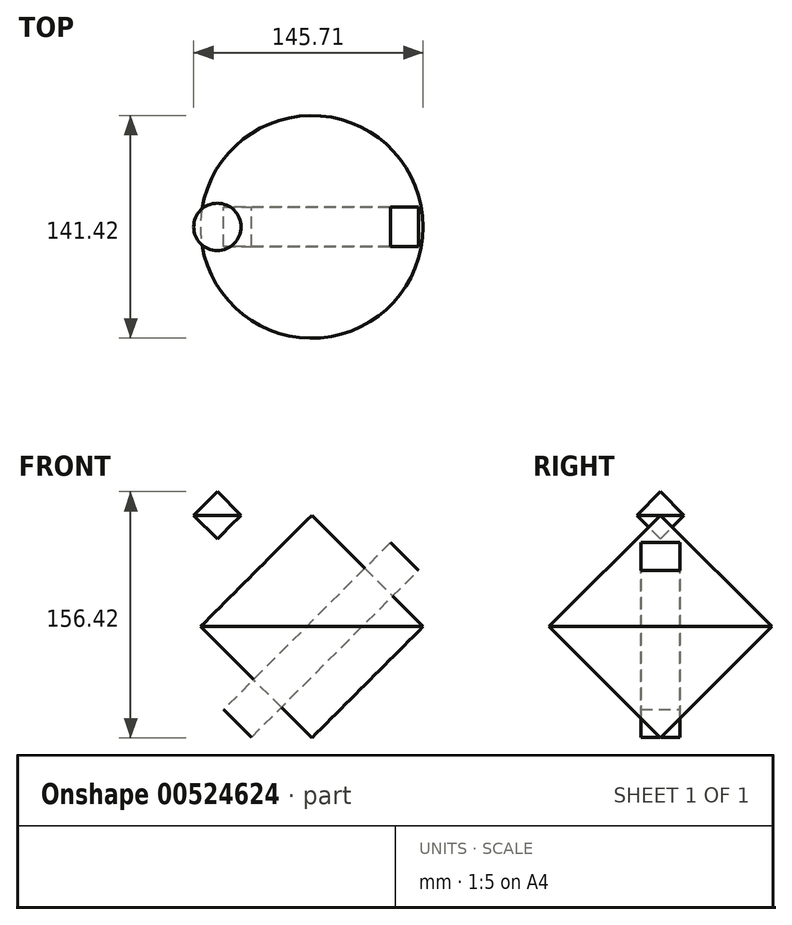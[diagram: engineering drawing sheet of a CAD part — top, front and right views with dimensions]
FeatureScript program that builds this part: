
annotation { "Feature Type Name" : "Feature", "Feature Type Description" : "" }
export const myFeature = defineFeature(function(context is Context, id is Id, definition is map)
    precondition{}
    {
        {
            var Q0;
            Q0=qCreatedBy(makeId("Front.planeOp"),FACE);
            var sketch = newSketch(context, id + "F0", { "sketchPlane" : qUnion([Q0])});
            skLineSegment(sketch, "E0", {"start": v(0, 80.4) * mm, "end": v(0, -82.74) * mm, "construction": true});
            skLineSegment(sketch, "E1", {"start": v(0, 70.71) * mm, "end": v(-70.71, 0) * mm});
            skLineSegment(sketch, "E2", {"start": v(-70.71, 0) * mm, "end": v(0, -70.71) * mm});
            skLineSegment(sketch, "E3", {"start": v(0, -70.71) * mm, "end": v(0, 70.71) * mm});
            skSolve(sketch);
        }
        {
            var Q0;
            Q0 = qSketchRegion(id + "F0", true);
            var Q1;
            Q1=sQuery(id+"F0.wireOp",EDGE,"E0");
            revolve(context, id + "F1", {"entities" : qUnion([Q0]), "axis" : qUnion([Q1]), "revolveType" : RevolveType.FULL});
        }
        {
            var Q0;
            Q0=qCreatedBy(makeId("Front.planeOp"),FACE);
            var sketch = newSketch(context, id + "F2", { "sketchPlane" : qUnion([Q0])});
            skLineSegment(sketch, "E4", {"start": v(-45, 70.71) * mm, "end": v(-60, 55.71) * mm});
            skLineSegment(sketch, "E5", {"start": v(-60, 55.71) * mm, "end": v(-60, 85.71) * mm});
            skLineSegment(sketch, "E6", {"start": v(-60, 85.71) * mm, "end": v(-45, 70.71) * mm});
            skLineSegment(sketch, "E7", {"start": v(-60, 47.19) * mm, "end": v(-60, 91.17) * mm, "construction": true});
            skSolve(sketch);
        }
        {
            var Q0;
            Q0=makeQuery(id+"F2.imprint","IMPRINT",FACE,{"disambiguationData":[TD([[makeQuery(id+"F2.imprint","IMPRINT",EDGE,{"derivedFrom":sQuery(id+"F2.wireOp",EDGE,"E4")}),-1.0]])]});
            var Q1;
            Q1=sQuery(id+"F2.wireOp",EDGE,"E7");
            revolve(context, id + "F3", {"entities" : qUnion([Q0]), "axis" : qUnion([Q1]), "revolveType" : RevolveType.FULL});
        }
        {
            var Q0;
            Q0=qCreatedBy(makeId("Front.planeOp"),FACE);
            var sketch = newSketch(context, id + "F4", { "sketchPlane" : qUnion([Q0])});
            skLineSegment(sketch, "E8", {"start": v(50, 53.39) * mm, "end": v(-56.07, -52.68) * mm});
            skLineSegment(sketch, "E9", {"start": v(-56.07, -52.68) * mm, "end": v(-38.39, -70.36) * mm});
            skLineSegment(sketch, "E10", {"start": v(-38.39, -70.36) * mm, "end": v(67.68, 35.71) * mm});
            skLineSegment(sketch, "E11", {"start": v(67.68, 35.71) * mm, "end": v(50, 53.39) * mm});
            skLineSegment(sketch, "E12", {"start": v(-55.42, -15.3) * mm, "end": v(-70.71, 0) * mm});
            skSolve(sketch);
        }
        {
            var Q0;
            Q0 = qSketchRegion(id + "F4", true);
            extrude(context, id + "F5", {"entities" : qUnion([Q0]), "endBound" : BoundingType.SYMMETRIC, "depth" : 25 * mm, "offsetDistance" : 25 * mm});
        }
    });
